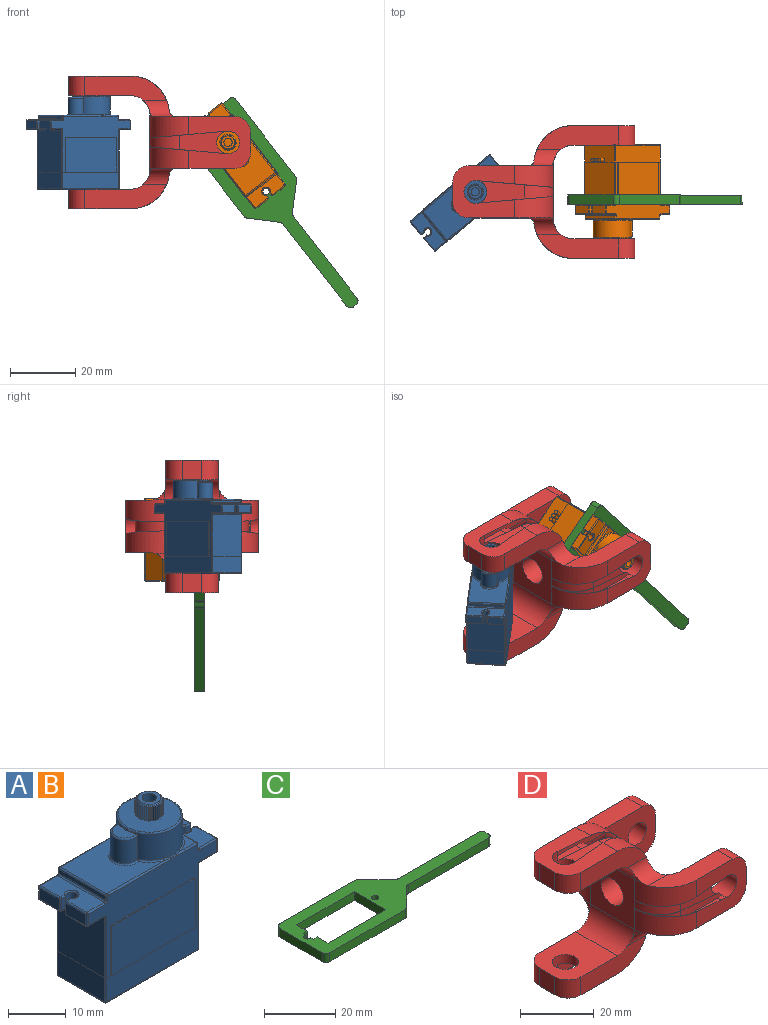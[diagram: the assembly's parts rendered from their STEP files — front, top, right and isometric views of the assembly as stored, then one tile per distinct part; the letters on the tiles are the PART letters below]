
ASSEMBLY  parts=4 mates=5
PART A: 240 faces, bbox 32.2x12.8x32.5 mm
  f0: plane 31.6x17.3mm, normal (0,-1,0), area 193.9mm2, adj f9,f42,f46,f51,f52,f61,f70,f74
  f1: plane 12.8x11.4mm, normal (1,0,0), area 145.9mm2, adj f17,f121,f130,f131
  f2: cylinder r=0.3mm len=5.1mm, axis (0,0,-1), area 2.4mm2, adj f9,f17,f130,f133
  f3: cylinder r=0.3mm len=5.1mm, axis (0,0,-1), area 2.4mm2, adj f8,f17,f131,f134
  f4: plane 31.6x17.3mm, normal (0,1,0), area 193.9mm2, adj f8,f43,f48,f55,f56,f64,f76,f77
  f5: plane 12.8x11.4mm, normal (-1,0,0), area 145.9mm2, adj f18,f114,f119,f123
  f6: cylinder r=0.3mm len=5.1mm, axis (0,0,-1), area 2.4mm2, adj f8,f18,f123,f128
  f7: cylinder r=0.3mm len=5.1mm, axis (0,0,-1), area 2.4mm2, adj f9,f18,f119,f125
  f8: plane 22.4x5.1mm, normal (0,1,0), area 114.2mm2, adj f3,f4,f6,f132
  f9: plane 22.4x5.1mm, normal (0,-1,0), area 114.2mm2, adj f0,f2,f7,f129
  f10: plane 3.67x3.67mm, normal (0,0,1), area 4.7mm2, adj f54,f55,f136
  f11: plane 14.17x11.4mm, normal (0,0,1), area 114.6mm2, adj f42,f43,f44,f143,f145,f147
  f12: plane 4.9x2.4mm, normal (1,0,0), area 11.8mm2, adj f97,f98,f111,f112
  f13: plane 4.9x2.4mm, normal (-1,0,0), area 11.8mm2, adj f68,f69,f90,f91
  f14: cylinder r=5.75mm len=11.5mm, axis (0,0,-1), area 170.5mm2, adj f28,f29,f136,f137,f138,f139,f140,f141
  f15: plane 11.4x4.25mm, normal (0,0,1), area 42mm2, adj f71,f72,f73,f75,f92,f93,f98,f99
  f16: plane 11.4x4.25mm, normal (0,0,1), area 42mm2, adj f49,f57,f58,f59,f69,f70,f77,f78
  f17: plane 11.4x5.1mm, normal (1,0,0), area 54.7mm2, adj f1,f2,f3,f36,f38,f40,f135
  f18: plane 11.4x5.1mm, normal (-1,0,0), area 58.1mm2, adj f5,f6,f7,f124
  f19: plane 22.4x11.4mm, normal (0,0,-1), area 255.4mm2, adj f124,f129,f132,f135
  f20: plane 11.4x4mm, normal (0,0,-1), area 39.1mm2, adj f85,f95,f96,f110,f111,f120,f121,f122
  f21: plane 4.9x2.4mm, normal (1,0,0), area 11.8mm2, adj f93,f94,f109,f110
  f22: plane 4.9x2.4mm, normal (-1,0,0), area 11.8mm2, adj f78,f79,f100,f101
  f23: plane 11.4x4mm, normal (0,0,-1), area 39.1mm2, adj f66,f67,f80,f90,f101,f108,f113,f114
  f24: plane 11.4x0.9mm, normal (1,0,0), area 10.3mm2, adj f47,f53,f54,f74,f75,f76
  f25: plane 11.4x0.9mm, normal (-1,0,0), area 10.3mm2, adj f44,f51,f56,f58
  f26: plane 3.67x3.67mm, normal (0,0,1), area 4.7mm2, adj f52,f53,f144
  f27: plane 10.9x10.9mm, normal (0,0,1), area 79.6mm2, adj f150,f153
  f28: cylinder r=2.5mm len=5mm, axis (0,0,-1), area 46.6mm2, adj f14,f145,f151
  f29: plane 4.4x2.89mm, normal (0,0,1), area 9.5mm2, adj f14,f151
  f30: cylinder r=1mm len=2.4mm, axis (0,0,1), area 12.6mm2, adj f31,f32,f49,f66
  f31: plane 2.4x1.08mm, normal (0,1,0), area 2.6mm2, adj f30,f57,f67,f68
  f32: plane 2.4x1.08mm, normal (0,-1,0), area 2.6mm2, adj f30,f59,f79,f80
  f33: plane 2.4x1.08mm, normal (0,-1,0), area 2.6mm2, adj f35,f73,f96,f97
  f34: plane 2.4x1.08mm, normal (0,1,0), area 2.6mm2, adj f35,f72,f94,f95
  f35: cylinder r=1mm len=2.4mm, axis (0,0,1), area 12.6mm2, adj f33,f34,f71,f85
  f36: cylinder r=0.6mm len=2mm, axis (-1,0,0), area 7.5mm2, adj f17,f37
  f37: plane 1.2x1.2mm, normal (1,0,0), area 1.1mm2, adj f36
  f38: cylinder r=0.6mm len=2mm, axis (-1,0,0), area 7.5mm2, adj f17,f39
  f39: plane 1.2x1.2mm, normal (1,0,0), area 1.1mm2, adj f38
  f40: cylinder r=0.6mm len=2mm, axis (-1,0,0), area 7.5mm2, adj f17,f41
  f41: plane 1.2x1.2mm, normal (1,0,0), area 1.1mm2, adj f40
  f42: cylinder r=0.3mm len=15.44mm, axis (1,0,0), area 7.2mm2, adj f0,f11,f45,f46,f149
  f43: cylinder r=0.3mm len=15.44mm, axis (-1,0,0), area 7.2mm2, adj f4,f11,f48,f50,f141
  f44: cylinder r=0.3mm len=11.4mm, axis (0,-1,0), area 5.4mm2, adj f11,f25,f45,f50
  f45: sphere r=0.3mm, area 0.2mm2, adj f42,f44,f51
  f46: bspline ~1.98x0.34mm, area 0.4mm2, adj f0,f42,f52,f148
  f47: bspline ~1.98x0.34mm, area 0.4mm2, adj f24,f53,f54,f140
  f48: bspline ~1.98x0.34mm, area 0.4mm2, adj f4,f43,f55,f139
  f49: torus R=1.3mm, axis (0,0,-1), area 2.7mm2, adj f16,f30,f57,f59
  f50: sphere r=0.3mm, area 0.2mm2, adj f43,f44,f56
  f51: cylinder r=0.3mm len=0.9mm, axis (0,0,-1), area 0.4mm2, adj f0,f25,f45,f61
  f52: cylinder r=0.3mm len=4.94mm, axis (1,0,0), area 2.2mm2, adj f0,f26,f46,f62,f146
  f53: cylinder r=0.3mm len=4.94mm, axis (0,1,0), area 2.2mm2, adj f24,f26,f47,f62,f142
  f54: cylinder r=0.3mm len=4.94mm, axis (0,1,0), area 2.2mm2, adj f10,f24,f47,f63,f138
  f55: cylinder r=0.3mm len=4.94mm, axis (-1,0,0), area 2.2mm2, adj f4,f10,f48,f63,f137
  f56: cylinder r=0.3mm len=0.9mm, axis (0,0,-1), area 0.4mm2, adj f4,f25,f50,f64
  f57: cylinder r=0.3mm len=1.08mm, axis (1,0,0), area 0.5mm2, adj f16,f31,f49,f60
  f58: cylinder r=0.3mm len=11.4mm, axis (0,1,0), area 5.4mm2, adj f16,f25,f61,f64
  f59: cylinder r=0.3mm len=1.08mm, axis (-1,0,0), area 0.5mm2, adj f16,f32,f49,f65
  f60: sphere r=0.3mm, area 0.2mm2, adj f57,f68,f69
  f61: torus R=0.6mm, axis (0,1,0), area 0.3mm2, adj f0,f51,f58,f70
  f62: sphere r=0.3mm, area 0.1mm2, adj f52,f53,f74
  f63: sphere r=0.3mm, area 0.1mm2, adj f54,f55,f76
  f64: torus R=0.6mm, axis (0,-1,0), area 0.3mm2, adj f4,f56,f58,f77
  f65: sphere r=0.3mm, area 0.2mm2, adj f59,f78,f79
  f66: torus R=1.3mm, axis (0,0,-1), area 2.7mm2, adj f23,f30,f67,f80
  f67: cylinder r=0.3mm len=1.08mm, axis (1,0,0), area 0.5mm2, adj f23,f31,f66,f81
  f68: cylinder r=0.3mm len=2.4mm, axis (0,0,1), area 1.1mm2, adj f13,f31,f60,f81
  f69: cylinder r=0.3mm len=4.9mm, axis (0,-1,0), area 2.3mm2, adj f13,f16,f60,f82
  f70: cylinder r=0.3mm len=4.25mm, axis (1,0,0), area 2mm2, adj f0,f16,f61,f82
  f71: torus R=1.3mm, axis (0,0,-1), area 2.7mm2, adj f15,f35,f72,f73
  f72: cylinder r=0.3mm len=1.08mm, axis (1,0,0), area 0.5mm2, adj f15,f34,f71,f84
  f73: cylinder r=0.3mm len=1.08mm, axis (-1,0,0), area 0.5mm2, adj f15,f33,f71,f86
  f74: cylinder r=0.3mm len=0.9mm, axis (0,0,-1), area 0.4mm2, adj f0,f24,f62,f83
  f75: cylinder r=0.3mm len=11.4mm, axis (0,-1,0), area 5.4mm2, adj f15,f24,f83,f87
  f76: cylinder r=0.3mm len=0.9mm, axis (0,0,-1), area 0.4mm2, adj f4,f24,f63,f87
  f77: cylinder r=0.3mm len=4.25mm, axis (-1,0,0), area 2mm2, adj f4,f16,f64,f88
  f78: cylinder r=0.3mm len=4.9mm, axis (0,-1,0), area 2.3mm2, adj f16,f22,f65,f88
  f79: cylinder r=0.3mm len=2.4mm, axis (0,0,1), area 1.1mm2, adj f22,f32,f65,f89
  f80: cylinder r=0.3mm len=1.08mm, axis (-1,0,0), area 0.5mm2, adj f23,f32,f66,f89
  f81: sphere r=0.3mm, area 0.1mm2, adj f67,f68,f90
  f82: sphere r=0.3mm, area 0.2mm2, adj f69,f70,f91
  f83: torus R=0.6mm, axis (0,1,0), area 0.3mm2, adj f0,f74,f75,f92
  f84: sphere r=0.3mm, area 0.1mm2, adj f72,f93,f94
  f85: torus R=1.3mm, axis (0,0,-1), area 2.7mm2, adj f20,f35,f95,f96
  f86: sphere r=0.3mm, area 0.1mm2, adj f73,f97,f98
  f87: torus R=0.6mm, axis (0,-1,0), area 0.3mm2, adj f4,f75,f76,f99
  f88: sphere r=0.3mm, area 0.2mm2, adj f77,f78,f100
  f89: sphere r=0.3mm, area 0.1mm2, adj f79,f80,f101
  f90: cylinder r=0.3mm len=4.9mm, axis (0,1,0), area 2.3mm2, adj f13,f23,f81,f102
  f91: cylinder r=0.3mm len=2.4mm, axis (0,0,-1), area 1.1mm2, adj f0,f13,f82,f102
  f92: cylinder r=0.3mm len=4.25mm, axis (1,0,0), area 2mm2, adj f0,f15,f83,f103
  f93: cylinder r=0.3mm len=4.9mm, axis (0,1,0), area 2.3mm2, adj f15,f21,f84,f103
  f94: cylinder r=0.3mm len=2.4mm, axis (0,0,1), area 1.1mm2, adj f21,f34,f84,f104
  f95: cylinder r=0.3mm len=1.08mm, axis (1,0,0), area 0.5mm2, adj f20,f34,f85,f104
  f96: cylinder r=0.3mm len=1.08mm, axis (-1,0,0), area 0.5mm2, adj f20,f33,f85,f105
  f97: cylinder r=0.3mm len=2.4mm, axis (0,0,-1), area 1.1mm2, adj f12,f33,f86,f105
  f98: cylinder r=0.3mm len=4.9mm, axis (0,1,0), area 2.3mm2, adj f12,f15,f86,f106
  f99: cylinder r=0.3mm len=4.25mm, axis (-1,0,0), area 2mm2, adj f4,f15,f87,f106
  f100: cylinder r=0.3mm len=2.4mm, axis (0,0,-1), area 1.1mm2, adj f4,f22,f88,f107
  f101: cylinder r=0.3mm len=4.9mm, axis (0,1,0), area 2.3mm2, adj f22,f23,f89,f107
  f102: sphere r=0.3mm, area 0.1mm2, adj f90,f91,f108
  f103: sphere r=0.3mm, area 0.1mm2, adj f92,f93,f109
  f104: sphere r=0.3mm, area 0.1mm2, adj f94,f95,f110
  f105: sphere r=0.3mm, area 0.1mm2, adj f96,f97,f111
  f106: sphere r=0.3mm, area 0.1mm2, adj f98,f99,f112
  f107: sphere r=0.3mm, area 0.1mm2, adj f100,f101,f113
  f108: cylinder r=0.3mm len=4mm, axis (-1,0,0), area 1.9mm2, adj f0,f23,f102,f115
  f109: cylinder r=0.3mm len=2.4mm, axis (0,0,-1), area 1.1mm2, adj f0,f21,f103,f116
  f110: cylinder r=0.3mm len=4.9mm, axis (0,-1,0), area 2.3mm2, adj f20,f21,f104,f116
  f111: cylinder r=0.3mm len=4.9mm, axis (0,-1,0), area 2.3mm2, adj f12,f20,f105,f117
  f112: cylinder r=0.3mm len=2.4mm, axis (0,0,-1), area 1.1mm2, adj f4,f12,f106,f117
  f113: cylinder r=0.3mm len=4mm, axis (1,0,0), area 1.9mm2, adj f4,f23,f107,f118
  f114: cylinder r=0.3mm len=11.4mm, axis (0,-1,0), area 5.4mm2, adj f5,f23,f115,f118
  f115: torus R=0.6mm, axis (0,1,0), area 0.3mm2, adj f0,f108,f114,f119
  f116: sphere r=0.3mm, area 0.1mm2, adj f109,f110,f120
  f117: sphere r=0.3mm, area 0.1mm2, adj f111,f112,f122
  f118: torus R=0.6mm, axis (0,-1,0), area 0.3mm2, adj f4,f113,f114,f123
  f119: cylinder r=0.3mm len=12.8mm, axis (0,0,-1), area 6mm2, adj f0,f5,f7,f115
  f120: cylinder r=0.3mm len=4mm, axis (-1,0,0), area 1.9mm2, adj f0,f20,f116,f126
  f121: cylinder r=0.3mm len=11.4mm, axis (0,1,0), area 5.4mm2, adj f1,f20,f126,f127
  f122: cylinder r=0.3mm len=4mm, axis (1,0,0), area 1.9mm2, adj f4,f20,f117,f127
  f123: cylinder r=0.3mm len=12.8mm, axis (0,0,-1), area 6mm2, adj f4,f5,f6,f118
  f124: cylinder r=0.3mm len=11.4mm, axis (0,1,0), area 5.4mm2, adj f18,f19,f125,f128
  f125: sphere r=0.3mm, area 0.1mm2, adj f7,f124,f129
  f126: torus R=0.6mm, axis (0,1,0), area 0.3mm2, adj f0,f120,f121,f130
  f127: torus R=0.6mm, axis (0,-1,0), area 0.3mm2, adj f4,f121,f122,f131
  f128: sphere r=0.3mm, area 0.1mm2, adj f6,f124,f132
  f129: cylinder r=0.3mm len=22.4mm, axis (-1,0,0), area 10.6mm2, adj f9,f19,f125,f133
  f130: cylinder r=0.3mm len=12.8mm, axis (0,0,-1), area 6mm2, adj f0,f1,f2,f126
  f131: cylinder r=0.3mm len=12.8mm, axis (0,0,-1), area 6mm2, adj f1,f3,f4,f127
  f132: cylinder r=0.3mm len=22.4mm, axis (1,0,0), area 10.6mm2, adj f8,f19,f128,f134
  f133: sphere r=0.3mm, area 0.1mm2, adj f2,f129,f135
  f134: sphere r=0.3mm, area 0.2mm2, adj f3,f132,f135
  f135: cylinder r=0.3mm len=11.4mm, axis (0,-1,0), area 5.4mm2, adj f17,f19,f133,f134
  f136: torus R=6.05mm, axis (0,0,-1), area 2.4mm2, adj f10,f14,f137,f138
  f137: bspline ~2.15x0.63mm, area 0.5mm2, adj f14,f55,f136,f139
  f138: bspline ~2.15x0.63mm, area 0.5mm2, adj f14,f54,f136,f140
  f139: bspline ~1.87x0.29mm, area 0.4mm2, adj f14,f48,f137,f141
  f140: bspline ~1.87x0.29mm, area 0.4mm2, adj f14,f47,f138,f142
  f141: bspline ~2.15x0.63mm, area 0.5mm2, adj f14,f43,f139,f143
  f142: bspline ~1.87x0.62mm, area 0.5mm2, adj f14,f53,f140,f144
  f143: torus R=6.05mm, axis (0,0,-1), area 2.2mm2, adj f11,f14,f141,f145
  f144: torus R=6.05mm, axis (0,0,-1), area 2.4mm2, adj f14,f26,f142,f146
  f145: torus R=2.8mm, axis (0,0,-1), area 4.6mm2, adj f11,f28,f143,f147
  f146: bspline ~2.15x0.63mm, area 0.5mm2, adj f14,f52,f144,f148
  f147: torus R=6.05mm, axis (0,0,-1), area 2.2mm2, adj f11,f14,f145,f149
  f148: bspline ~1.87x0.29mm, area 0.4mm2, adj f14,f46,f146,f149
  f149: bspline ~2.15x0.63mm, area 0.5mm2, adj f14,f42,f147,f148
  f150: torus R=5.45mm, axis (0,0,1), area 16.7mm2, adj f14,f27
  f151: torus R=2.2mm, axis (0,0,1), area 4.3mm2, adj f14,f28,f29
  f152: plane 4.98x4.98mm, normal (0,0,-1), area 3.5mm2, adj f153,f156,f157,f158,f159,f160,f161,f162
  f153: cylinder r=2.09mm len=4.18mm, axis (0,0,1), area 3.9mm2, adj f27,f152
  f154: plane 4x4mm, normal (0,0,1), area 7.7mm2, adj f155,f238
  f155: cone r=2mm half-angle=45deg, axis (0,0,-1), area 6.8mm2, adj f154,f156,f157,f158,f159,f160,f161,f162
  f156: plane 3.01x0.31mm, normal (0.8,0.6,0), area 1mm2, adj f152,f155,f157,f163
  f157: plane 3.01x0.31mm, normal (-0.8,0.6,0), area 1mm2, adj f152,f155,f156,f226
  f158: plane 3.01x0.35mm, normal (0.39,0.92,0), area 1mm2, adj f152,f155,f159,f167
  f159: plane 3.01x0.38mm, normal (-0.99,0.12,0), area 1mm2, adj f152,f155,f158,f160
  f160: plane 3.01x0.32mm, normal (0.55,0.84,0), area 1mm2, adj f152,f155,f159,f161
  f161: plane 3.01x0.36mm, normal (-0.96,0.29,0), area 1mm2, adj f152,f155,f160,f162
  f162: plane 3.01x0.28mm, normal (0.68,0.73,0), area 1mm2, adj f152,f155,f161,f163
  f163: plane 3.01x0.34mm, normal (-0.89,0.45,0), area 1mm2, adj f152,f155,f156,f162
  f164: plane 3.01x0.38mm, normal (0.05,1,0), area 1mm2, adj f152,f155,f165,f171
  f165: plane 3.01x0.37mm, normal (-0.97,-0.23,0), area 1mm2, adj f152,f155,f164,f166
  f166: plane 3.01x0.37mm, normal (0.23,0.97,0), area 1mm2, adj f152,f155,f165,f167
  f167: plane 3.01x0.38mm, normal (-1,-0.05,0), area 1mm2, adj f152,f155,f158,f166
  f168: plane 3.01x0.36mm, normal (-0.29,0.96,0), area 1mm2, adj f152,f155,f169,f175
  f169: plane 3.01x0.32mm, normal (-0.84,-0.55,0), area 1mm2, adj f152,f155,f168,f170
  f170: plane 3.01x0.38mm, normal (-0.12,0.99,0), area 1mm2, adj f152,f155,f169,f171
  f171: plane 3.01x0.35mm, normal (-0.92,-0.39,0), area 1mm2, adj f152,f155,f164,f170
  f172: plane 3.01x0.31mm, normal (-0.6,0.8,0), area 1mm2, adj f152,f155,f173,f179
  f173: plane 3.01x0.31mm, normal (-0.6,-0.8,0), area 1mm2, adj f152,f155,f172,f174
  f174: plane 3.01x0.34mm, normal (-0.45,0.89,0), area 1mm2, adj f152,f155,f173,f175
  f175: plane 3.01x0.28mm, normal (-0.73,-0.68,0), area 1mm2, adj f152,f155,f168,f174
  f176: plane 3.01x0.32mm, normal (-0.84,0.55,0), area 1mm2, adj f152,f155,f177,f189
  f177: plane 3.01x0.36mm, normal (-0.29,-0.96,0), area 1mm2, adj f152,f155,f176,f178
  f178: plane 3.01x0.28mm, normal (-0.73,0.68,0), area 1mm2, adj f152,f155,f177,f179
  f179: plane 3.01x0.34mm, normal (-0.45,-0.89,0), area 1mm2, adj f152,f155,f172,f178
  f180: plane 3.01x0.37mm, normal (0.23,-0.97,0), area 1mm2, adj f152,f155,f181,f186
  f181: plane 3.01x0.38mm, normal (-1,0.05,0), area 1mm2, adj f152,f155,f180,f183
  f182: plane 3.01x0.38mm, normal (-0.99,-0.12,0), area 1mm2, adj f152,f155,f183,f185
  f183: plane 3.01x0.35mm, normal (0.39,-0.92,0), area 1mm2, adj f152,f155,f181,f182
  f184: plane 3.01x0.36mm, normal (-0.96,-0.29,0), area 1mm2, adj f152,f155,f185,f193
  f185: plane 3.01x0.32mm, normal (0.55,-0.84,0), area 1mm2, adj f152,f155,f182,f184
  f186: plane 3.01x0.37mm, normal (-0.97,0.23,0), area 1mm2, adj f152,f155,f180,f187
  f187: plane 3.01x0.38mm, normal (0.05,-1,0), area 1mm2, adj f152,f155,f186,f188
  f188: plane 3.01x0.35mm, normal (-0.92,0.39,0), area 1mm2, adj f152,f155,f187,f189
  f189: plane 3.01x0.38mm, normal (-0.12,-0.99,0), area 1mm2, adj f152,f155,f176,f188
  f190: plane 3.01x0.31mm, normal (-0.8,-0.6,0), area 1mm2, adj f152,f155,f191,f197
  f191: plane 3.01x0.31mm, normal (0.8,-0.6,0), area 1mm2, adj f152,f155,f190,f192
  f192: plane 3.01x0.34mm, normal (-0.89,-0.45,0), area 1mm2, adj f152,f155,f191,f193
  f193: plane 3.01x0.28mm, normal (0.68,-0.73,0), area 1mm2, adj f152,f155,f184,f192
  f194: plane 3.01x0.32mm, normal (-0.55,-0.84,0), area 1mm2, adj f152,f155,f195,f201
  f195: plane 3.01x0.36mm, normal (0.96,-0.29,0), area 1mm2, adj f152,f155,f194,f196
  f196: plane 3.01x0.28mm, normal (-0.68,-0.73,0), area 1mm2, adj f152,f155,f195,f197
  f197: plane 3.01x0.34mm, normal (0.89,-0.45,0), area 1mm2, adj f152,f155,f190,f196
  f198: plane 3.01x0.37mm, normal (-0.23,-0.97,0), area 1mm2, adj f152,f155,f199,f205
  f199: plane 3.01x0.38mm, normal (1,0.05,0), area 1mm2, adj f152,f155,f198,f200
  f200: plane 3.01x0.35mm, normal (-0.39,-0.92,0), area 1mm2, adj f152,f155,f199,f201
  f201: plane 3.01x0.38mm, normal (0.99,-0.12,0), area 1mm2, adj f152,f155,f194,f200
  f202: plane 3.01x0.38mm, normal (0.12,-0.99,0), area 1mm2, adj f152,f155,f203,f209
  f203: plane 3.01x0.35mm, normal (0.92,0.39,0), area 1mm2, adj f152,f155,f202,f204
  f204: plane 3.01x0.38mm, normal (-0.05,-1,0), area 1mm2, adj f152,f155,f203,f205
  f205: plane 3.01x0.37mm, normal (0.97,0.23,0), area 1mm2, adj f152,f155,f198,f204
  f206: plane 3.01x0.34mm, normal (0.45,-0.89,0), area 1mm2, adj f152,f155,f207,f217
  f207: plane 3.01x0.28mm, normal (0.73,0.68,0), area 1mm2, adj f152,f155,f206,f208
  f208: plane 3.01x0.36mm, normal (0.29,-0.96,0), area 1mm2, adj f152,f155,f207,f209
  f209: plane 3.01x0.32mm, normal (0.84,0.55,0), area 1mm2, adj f152,f155,f202,f208
  f210: plane 3.01x0.28mm, normal (0.73,-0.68,0), area 1mm2, adj f152,f155,f211,f215
  f211: plane 3.01x0.34mm, normal (0.45,0.89,0), area 1mm2, adj f152,f155,f210,f216
  f212: plane 3.01x0.35mm, normal (0.92,-0.39,0), area 1mm2, adj f152,f155,f213,f225
  f213: plane 3.01x0.38mm, normal (0.12,0.99,0), area 1mm2, adj f152,f155,f212,f214
  f214: plane 3.01x0.32mm, normal (0.84,-0.55,0), area 1mm2, adj f152,f155,f213,f215
  f215: plane 3.01x0.36mm, normal (0.29,0.96,0), area 1mm2, adj f152,f155,f210,f214
  f216: plane 3.01x0.31mm, normal (0.6,-0.8,0), area 1mm2, adj f152,f155,f211,f217
  f217: plane 3.01x0.31mm, normal (0.6,0.8,0), area 1mm2, adj f152,f155,f206,f216
  f218: plane 3.01x0.38mm, normal (1,-0.05,0), area 1mm2, adj f152,f155,f219,f223
  f219: plane 3.01x0.37mm, normal (-0.23,0.97,0), area 1mm2, adj f152,f155,f218,f224
  f220: plane 3.01x0.36mm, normal (0.96,0.29,0), area 1mm2, adj f152,f155,f221,f227
  f221: plane 3.01x0.32mm, normal (-0.55,0.84,0), area 1mm2, adj f152,f155,f220,f222
  f222: plane 3.01x0.38mm, normal (0.99,0.12,0), area 1mm2, adj f152,f155,f221,f223
  f223: plane 3.01x0.35mm, normal (-0.39,0.92,0), area 1mm2, adj f152,f155,f218,f222
  f224: plane 3.01x0.37mm, normal (0.97,-0.23,0), area 1mm2, adj f152,f155,f219,f225
  f225: plane 3.01x0.38mm, normal (-0.05,1,0), area 1mm2, adj f152,f155,f212,f224
  f226: plane 3.01x0.34mm, normal (0.89,0.45,0), area 1mm2, adj f152,f155,f157,f227
  f227: plane 3.01x0.28mm, normal (-0.68,0.73,0), area 1mm2, adj f152,f155,f220,f226
  f228: plane 10.5x0.2mm, normal (1,0,0), area 2.1mm2, adj f0,f229,f231,f232
  f229: plane 20.5x0.2mm, normal (0,0,1), area 4.1mm2, adj f0,f228,f230,f232
  f230: plane 10.5x0.2mm, normal (-1,0,0), area 2.1mm2, adj f0,f229,f231,f232
  f231: plane 20.5x0.2mm, normal (0,0,-1), area 4.1mm2, adj f0,f228,f230,f232
  f232: plane 20.5x10.5mm, normal (0,-1,0), area 215.3mm2, adj f228,f229,f230,f231
  f233: plane 20.5x0.2mm, normal (0,0,-1), area 4.1mm2, adj f4,f234,f236,f237
  f234: plane 10.5x0.2mm, normal (-1,0,0), area 2.1mm2, adj f4,f233,f235,f237
  f235: plane 20.5x0.2mm, normal (0,0,1), area 4.1mm2, adj f4,f234,f236,f237
  f236: plane 10.5x0.2mm, normal (1,0,0), area 2.1mm2, adj f4,f233,f235,f237
  f237: plane 20.5x10.5mm, normal (0,1,0), area 215.3mm2, adj f233,f234,f235,f236
  f238: cylinder r=1.25mm len=2.5mm, axis (0,0,1), area 19.6mm2, adj f154,f239
  f239: plane 2.5x2.5mm, normal (0,0,1), area 4.9mm2, adj f238
PART B: same geometry as A
PART C: 29 faces, bbox 74x20x3 mm
  f0: plane 3x1.13mm, normal (1,0,0), area 3.4mm2, adj f2,f3,f26,f27
  f1: plane 4.25x3mm, normal (1,0,0), area 12.7mm2, adj f2,f3,f12,f26
  f2: plane 74x20mm, normal (0,0,1), area 570.9mm2, adj f0,f1,f4,f5,f6,f7,f8,f9
  f3: plane 74x20mm, normal (0,0,-1), area 570.9mm2, adj f0,f1,f4,f5,f6,f7,f8,f9
  f4: plane 17x3mm, normal (-1,0,0), area 51mm2, adj f2,f3,f18,f23
  f5: plane 29.88x3mm, normal (0,-1,0), area 89.6mm2, adj f2,f3,f18,f19
  f6: plane 31.88x3mm, normal (0,-1,0), area 95.6mm2, adj f2,f3,f16,f20
  f7: plane 3x1mm, normal (1,0,0), area 3mm2, adj f2,f3,f20,f21
  f8: plane 31.88x3mm, normal (0,1,0), area 95.6mm2, adj f2,f3,f17,f21
  f9: plane 4.25x3mm, normal (1,0,0), area 12.8mm2, adj f2,f3,f10,f24
  f10: plane 23x3mm, normal (0,-1,0), area 69mm2, adj f2,f3,f9,f11
  f11: plane 12.5x3mm, normal (-1,0,0), area 37.5mm2, adj f2,f3,f10,f12
  f12: plane 23x3mm, normal (0,1,0), area 69mm2, adj f1,f2,f3,f11
  f13: plane 29.88x3mm, normal (0,1,0), area 89.6mm2, adj f2,f3,f22,f23
  f14: plane 7.12x7.12mm, normal (0.71,0.71,0), area 30.2mm2, adj f2,f3,f17,f22
  f15: plane 7.12x7.12mm, normal (0.71,-0.71,0), area 30.2mm2, adj f2,f3,f16,f19
  f16: cylinder r=1.5mm len=3mm, axis (0,0,-1), area 3.5mm2, adj f2,f3,f6,f15
  f17: cylinder r=1.5mm len=3mm, axis (0,0,1), area 3.5mm2, adj f2,f3,f8,f14
  f18: cylinder r=1.5mm len=3mm, axis (0,0,1), area 7.1mm2, adj f2,f3,f4,f5
  f19: cylinder r=1.5mm len=3mm, axis (0,0,1), area 3.5mm2, adj f2,f3,f5,f15
  f20: cylinder r=1.5mm len=3mm, axis (0,0,-1), area 7.1mm2, adj f2,f3,f6,f7
  f21: cylinder r=1.5mm len=3mm, axis (0,0,1), area 7.1mm2, adj f2,f3,f7,f8
  f22: cylinder r=1.5mm len=3mm, axis (0,0,1), area 3.5mm2, adj f2,f3,f13,f14
  f23: cylinder r=1.5mm len=3mm, axis (0,0,-1), area 7.1mm2, adj f2,f3,f4,f13
  f24: plane 3x1.5mm, normal (0,-1,0), area 4.5mm2, adj f2,f3,f9,f25
  f25: plane 3x1.13mm, normal (1,0,0), area 3.4mm2, adj f2,f3,f24,f27
  f26: plane 3x1.5mm, normal (0,1,0), area 4.5mm2, adj f0,f1,f2,f3
  f27: cylinder r=1mm len=3mm, axis (0,0,1), area 12.6mm2, adj f0,f2,f3,f25
  f28: cylinder r=1mm len=3mm, axis (0,0,1), area 18.8mm2, adj f2,f3
PART D: 75 faces, bbox 56x40.8x40.8 mm
  f0: cylinder r=12mm len=12mm, axis (0,1,0), area 118.5mm2, adj f13,f22,f23,f34,f39,f59
  f1: cylinder r=12mm len=12mm, axis (0,0,1), area 118.5mm2, adj f8,f9,f10,f34,f44,f62
  f2: cylinder r=12mm len=12mm, axis (0,-1,0), area 118.5mm2, adj f13,f25,f28,f31,f43,f65
  f3: cylinder r=12mm len=12mm, axis (0,0,-1), area 118.5mm2, adj f4,f10,f16,f31,f49,f68
  f4: plane 19x16mm, normal (0,-1,0), area 202.6mm2, adj f3,f11,f16,f17,f19,f48,f54,f56
  f5: cylinder r=3.5mm len=7mm, axis (0,0,1), area 102.6mm2, adj f20,f22,f58,f59,f60
  f6: cylinder r=12mm len=12mm, axis (0,1,0), area 118.5mm2, adj f13,f22,f24,f33,f40,f58
  f7: plane 25.08x7.4mm, normal (0,0,1), area 139.6mm2, adj f9,f14,f32,f38,f45,f57
  f8: plane 25.08x7.4mm, normal (0,0,-1), area 139.6mm2, adj f1,f9,f14,f34,f38,f55
  f9: plane 19x16mm, normal (0,1,0), area 202.6mm2, adj f1,f7,f8,f15,f18,f45,f55,f57
  f10: plane 16.8x16.8mm, normal (-1,0,0), area 225.5mm2, adj f1,f3,f35,f36,f45,f48,f70,f72
  f11: plane 6x6mm, normal (1,0,0), area 36mm2, adj f4,f12,f54,f56
  f12: plane 19x16mm, normal (0,1,0), area 254.8mm2, adj f11,f16,f17,f19,f37,f54,f56
  f13: plane 16.8x16.8mm, normal (1,0,0), area 225.5mm2, adj f0,f2,f6,f37,f38,f42,f71,f73
  f14: plane 19x16mm, normal (0,-1,0), area 254.8mm2, adj f7,f8,f15,f18,f38,f55,f57
  f15: plane 6x6mm, normal (1,0,0), area 36mm2, adj f9,f14,f55,f57
  f16: plane 25.08x7.4mm, normal (0,0,1), area 139.6mm2, adj f3,f4,f12,f31,f37,f56
  f17: plane 25.08x7.4mm, normal (0,0,-1), area 139.6mm2, adj f4,f12,f33,f37,f48,f54
  f18: cylinder r=3.5mm len=7mm, axis (0,-1,0), area 102.6mm2, adj f9,f14,f61,f62,f63
  f19: cylinder r=3.5mm len=7mm, axis (0,-1,0), area 102.6mm2, adj f4,f12,f67,f68,f69
  f20: plane 19x16mm, normal (0,0,1), area 254.8mm2, adj f5,f21,f23,f24,f36,f50,f52
  f21: plane 6x6mm, normal (-1,0,0), area 36mm2, adj f20,f22,f50,f52
  f22: plane 19x16mm, normal (0,0,-1), area 202.6mm2, adj f0,f5,f6,f21,f23,f24,f50,f52
  f23: plane 25.08x7.4mm, normal (0,1,0), area 139.6mm2, adj f0,f20,f22,f34,f36,f50
  f24: plane 25.08x7.4mm, normal (0,-1,0), area 139.6mm2, adj f6,f20,f22,f33,f36,f52
  f25: plane 19x16mm, normal (0,0,1), area 202.6mm2, adj f2,f26,f28,f29,f30,f42,f51,f53
  f26: plane 6x6mm, normal (-1,0,0), area 36mm2, adj f25,f27,f51,f53
  f27: plane 19x16mm, normal (0,0,-1), area 254.8mm2, adj f26,f28,f29,f30,f35,f51,f53
  f28: plane 25.08x7.4mm, normal (0,-1,0), area 139.6mm2, adj f2,f25,f27,f31,f35,f53
  f29: plane 25.08x7.4mm, normal (0,1,0), area 139.6mm2, adj f25,f27,f32,f35,f42,f51
  f30: cylinder r=3.5mm len=7mm, axis (0,0,1), area 102.6mm2, adj f25,f27,f64,f65,f66
  f31: cylinder r=5mm len=10.3mm, axis (-1,0,0), area 50.5mm2, adj f2,f3,f16,f28,f35,f37,f43,f49
  f32: cylinder r=5mm len=10.3mm, axis (1,0,0), area 50.5mm2, adj f7,f29,f35,f38,f41,f42,f45,f46
  f33: cylinder r=5mm len=10.3mm, axis (1,0,0), area 50.5mm2, adj f6,f17,f24,f36,f37,f40,f47,f48
  f34: cylinder r=5mm len=10.3mm, axis (-1,0,0), area 50.5mm2, adj f0,f1,f8,f23,f36,f38,f39,f44
  f35: cylinder r=6mm len=16.8mm, axis (0,-1,0), area 153.6mm2, adj f10,f27,f28,f29,f31,f32,f46,f49
  f36: cylinder r=6mm len=16.8mm, axis (0,1,0), area 153.6mm2, adj f10,f20,f23,f24,f33,f34,f44,f47
  f37: cylinder r=6mm len=16.8mm, axis (0,0,1), area 153.6mm2, adj f12,f13,f16,f17,f31,f33,f40,f43
  f38: cylinder r=6mm len=16.8mm, axis (0,0,-1), area 153.6mm2, adj f7,f8,f13,f14,f32,f34,f39,f41
  f39: torus R=18mm, axis (0,0,1), area 2.6mm2, adj f0,f34,f38
  f40: torus R=18mm, axis (0,0,1), area 2.6mm2, adj f6,f33,f37
  f41: torus R=18mm, axis (0,0,1), area 2.6mm2, adj f32,f38,f42
  f42: cylinder r=12mm len=12mm, axis (0,-1,0), area 118.5mm2, adj f13,f25,f29,f32,f41,f64
  f43: torus R=18mm, axis (0,0,1), area 2.6mm2, adj f2,f31,f37
  f44: torus R=18mm, axis (0,1,0), area 2.6mm2, adj f1,f34,f36
  f45: cylinder r=12mm len=12mm, axis (0,0,1), area 118.5mm2, adj f7,f9,f10,f32,f46,f61
  f46: torus R=18mm, axis (0,1,0), area 2.6mm2, adj f32,f35,f45
  f47: torus R=18mm, axis (0,1,0), area 2.6mm2, adj f33,f36,f48
  f48: cylinder r=12mm len=12mm, axis (0,0,-1), area 118.5mm2, adj f4,f10,f17,f33,f47,f67
  f49: torus R=18mm, axis (0,1,0), area 2.6mm2, adj f3,f31,f35
  f50: cylinder r=5mm len=6mm, axis (0,0,-1), area 47.1mm2, adj f20,f21,f22,f23
  f51: cylinder r=5mm len=6mm, axis (0,0,-1), area 47.1mm2, adj f25,f26,f27,f29
  f52: cylinder r=5mm len=6mm, axis (0,0,1), area 47.1mm2, adj f20,f21,f22,f24
  f53: cylinder r=5mm len=6mm, axis (0,0,1), area 47.1mm2, adj f25,f26,f27,f28
  f54: cylinder r=5mm len=6mm, axis (0,1,0), area 47.1mm2, adj f4,f11,f12,f17
  f55: cylinder r=5mm len=6mm, axis (0,1,0), area 47.1mm2, adj f8,f9,f14,f15
  f56: cylinder r=5mm len=6mm, axis (0,-1,0), area 47.1mm2, adj f4,f11,f12,f16
  f57: cylinder r=5mm len=6mm, axis (0,-1,0), area 47.1mm2, adj f7,f9,f14,f15
  f58: plane 23.39x12mm, normal (-0.09,1,0), area 56.9mm2, adj f5,f6,f22,f60,f73
  f59: plane 23.39x12mm, normal (-0.09,-1,0), area 56.9mm2, adj f0,f5,f22,f60,f73
  f60: plane 14.39x6.89mm, normal (0,0,-1), area 66.1mm2, adj f5,f58,f59,f73
  f61: plane 23.39x12mm, normal (0.09,0,-1), area 56.9mm2, adj f9,f18,f45,f63,f72
  f62: plane 23.39x12mm, normal (0.09,0,1), area 56.9mm2, adj f1,f9,f18,f63,f72
  f63: plane 14.39x6.89mm, normal (0,1,0), area 66.1mm2, adj f18,f61,f62,f72
  f64: plane 23.39x12mm, normal (-0.09,-1,0), area 56.9mm2, adj f25,f30,f42,f66,f71
  f65: plane 23.39x12mm, normal (-0.09,1,0), area 56.9mm2, adj f2,f25,f30,f66,f71
  f66: plane 14.39x6.89mm, normal (0,0,1), area 66.1mm2, adj f30,f64,f65,f71
  f67: plane 23.39x12mm, normal (0.09,0,1), area 56.9mm2, adj f4,f19,f48,f69,f70
  f68: plane 23.39x12mm, normal (0.09,0,-1), area 56.9mm2, adj f3,f4,f19,f69,f70
  f69: plane 14.39x6.89mm, normal (0,-1,0), area 66.1mm2, adj f19,f67,f68,f70
  f70: cylinder r=9mm len=9mm, axis (0,0,-1), area 47.7mm2, adj f10,f67,f68,f69
  f71: cylinder r=9mm len=9mm, axis (0,-1,0), area 47.7mm2, adj f13,f64,f65,f66
  f72: cylinder r=9mm len=9mm, axis (0,0,1), area 47.7mm2, adj f10,f61,f62,f63
  f73: cylinder r=9mm len=9mm, axis (0,1,0), area 47.7mm2, adj f13,f58,f59,f60
  f74: cylinder r=4.25mm len=8.5mm, axis (1,0,0), area 160.2mm2, adj f10,f13
PLACE A rot(axis=(0,0,1),40deg) t=(34.5,26.93,0.25)mm
PLACE B rot(axis=(0.33,-0.67,0.67),143.7deg) t=(83.74,44.91,10.7)mm
PLACE C rot(axis=(0.82,0.4,-0.4),101.2deg) t=(83.95,29.41,10.42)mm
PLACE D t=(72.84,30.31,6.85)mm
MATE revolute D.f5 <-> A.f14  axis (0,0,-1) through (38.52,30.31,29.25)mm
MATE revolute D.f18 <-> B.f14  axis (0,-1,0) through (80.52,15.91,14.85)mm
MATE parallel C.f13 <-> B.f0  axis (0.79,0,0.61) through (92.13,27.91,16.2)mm
MATE revolute B.f30 <-> C.f28  axis (0,1,0) through (92.23,26.41,-0.24)mm
MATE planar C.f28 <-> B.f23  axis (0,-1,0) through (92.23,26.41,-0.24)mm
